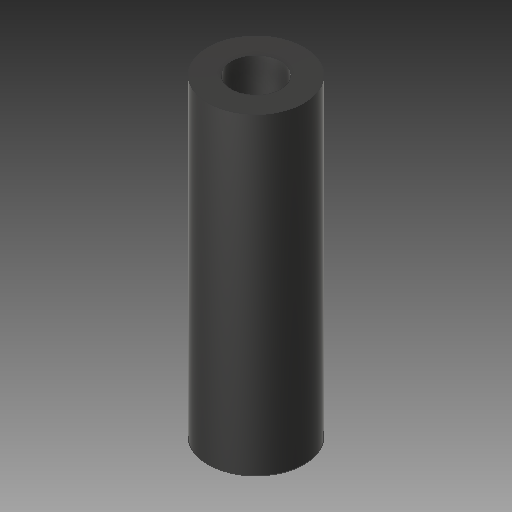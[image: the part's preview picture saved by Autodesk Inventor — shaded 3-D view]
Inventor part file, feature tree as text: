
AUTODESK INVENTOR PART (.ipt)
format: ipt  version: 2019 (Build 230136000, 136)  size: 101,888 bytes
history: native  units: mm
features: extrude x1, sketch x1
ambient origin geometry x8: Origin, YZ Plane, XZ Plane, XY Plane, X Axis, Y Axis, Z Axis, Center Point
bodies: Solid1 (feature_tree)
feature tree (2):
  extrude  "Extrusion1"  Depth=20.2mm
  sketch  "Sketch1"  dims[d0=6.2mm d1=3.2mm d2=20.2mm d3=0.0mm]
